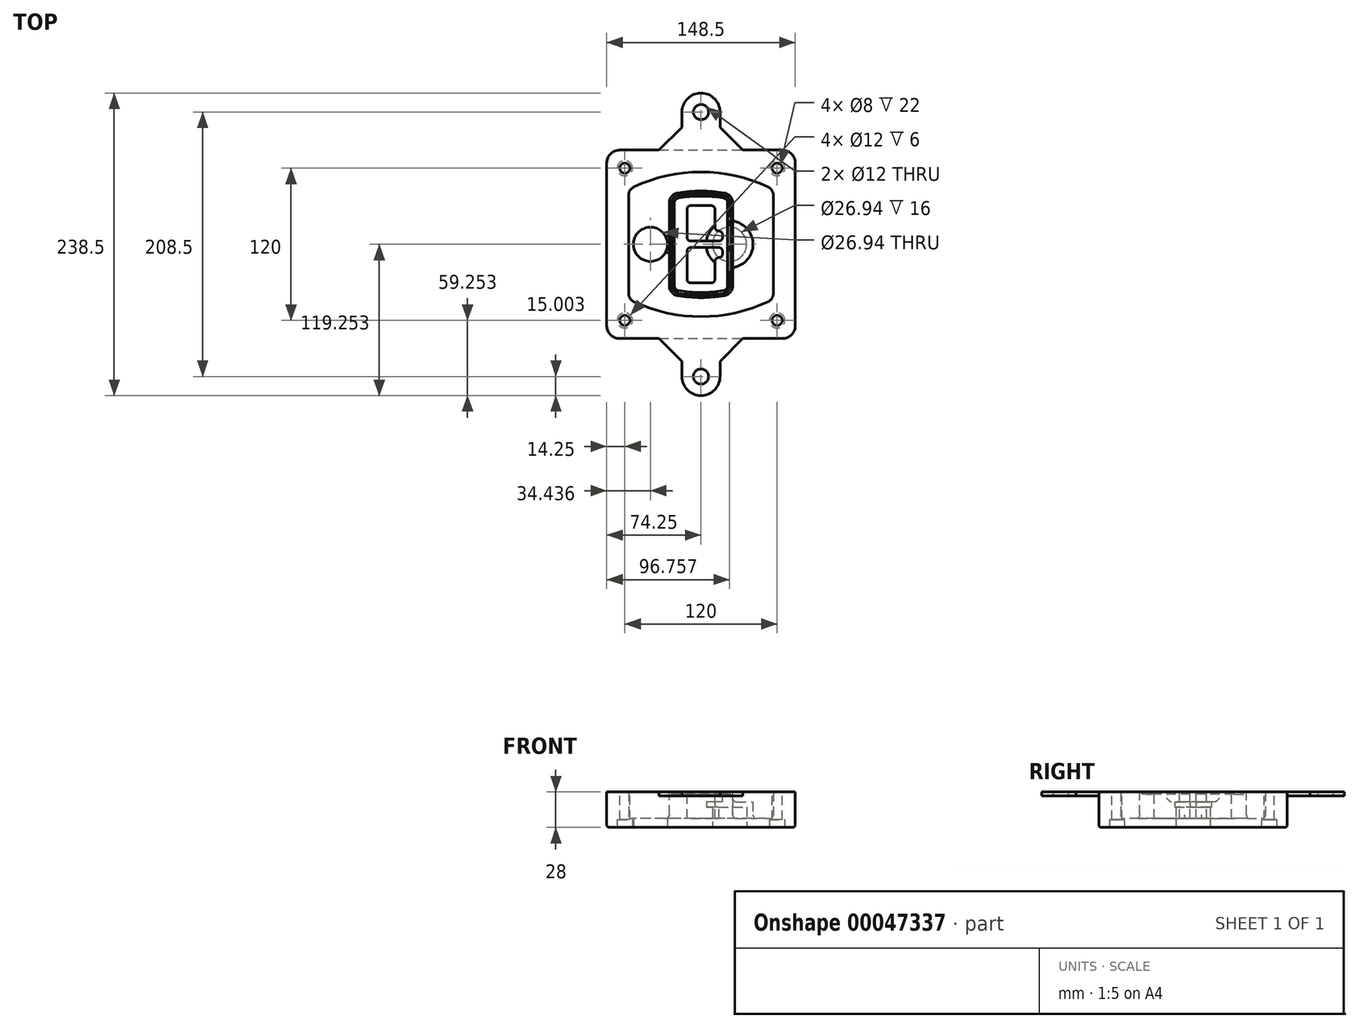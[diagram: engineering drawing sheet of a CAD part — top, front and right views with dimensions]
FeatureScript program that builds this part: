
annotation { "Feature Type Name" : "Feature", "Feature Type Description" : "" }
export const myFeature = defineFeature(function(context is Context, id is Id, definition is map)
    precondition{}
    {
        {
            var Q0;
            Q0=qCreatedBy(makeId("Top.planeOp"),FACE);
            var sketch = newSketch(context, id + "F0", { "sketchPlane" : qUnion([Q0])});
            skPoint(sketch, "E0.rect.middle", {"position": v(0, 0) * mm});
            skLineSegment(sketch, "E1.bottom", {"start": v(24.05, 28.38) * mm, "end": v(152.55, 28.38) * mm});
            skLineSegment(sketch, "E1.top", {"start": v(24.05, 176.88) * mm, "end": v(152.55, 176.88) * mm});
            skLineSegment(sketch, "E1.left", {"start": v(14.05, 38.38) * mm, "end": v(14.05, 166.88) * mm});
            skLineSegment(sketch, "E1.right", {"start": v(162.55, 38.38) * mm, "end": v(162.55, 166.88) * mm});
            skLineSegment(sketch, "E2", {"start": v(14.05, 176.88) * mm, "end": v(162.55, 28.38) * mm, "construction": true});
            skLineSegment(sketch, "E3", {"start": v(162.55, 176.88) * mm, "end": v(14.05, 28.38) * mm, "construction": true});
            skCircle(sketch, "E4", {"center": v(28.3, 162.63) * mm, "radius": 4 * mm});
            skCircle(sketch, "E5", {"center": v(148.3, 162.63) * mm, "radius": 4 * mm});
            skCircle(sketch, "E6", {"center": v(148.3, 42.63) * mm, "radius": 4 * mm});
            skCircle(sketch, "E7", {"center": v(28.3, 42.63) * mm, "radius": 4 * mm});
            skLineSegment(sketch, "E8", {"start": v(28.3, 162.63) * mm, "end": v(148.3, 162.63) * mm, "construction": true});
            skLineSegment(sketch, "E9", {"start": v(148.3, 162.63) * mm, "end": v(148.3, 42.63) * mm, "construction": true});
            skLineSegment(sketch, "E10", {"start": v(148.3, 42.63) * mm, "end": v(28.3, 42.63) * mm, "construction": true});
            skLineSegment(sketch, "E11", {"start": v(28.3, 42.63) * mm, "end": v(28.3, 162.63) * mm, "construction": true});
            skLineSegment(sketch, "E12", {"start": v(28.3, 141.46) * mm, "end": v(28.3, 63.8) * mm});
            skLineSegment(sketch, "E13", {"start": v(148.3, 141.46) * mm, "end": v(148.3, 63.8) * mm});
            skArc(sketch, "E14", {"start": v(142.56, 150.51) * mm, "mid": v(88.3, 162.63) * mm, "end": v(34.04, 150.51) * mm});
            skArc(sketch, "E15", {"start": v(34.04, 54.75) * mm, "mid": v(88.3, 42.63) * mm, "end": v(142.56, 54.75) * mm});
            skLineSegment(sketch, "E16", {"start": v(28.3, 102.63) * mm, "end": v(148.3, 102.63) * mm, "construction": true});
            skPoint(sketch, "E17.visualSharp", {"position": v(28.3, 57.63) * mm});
            skArc(sketch, "E17.filletArc", {"start": v(28.3, 63.8) * mm, "mid": v(29.86, 58.44) * mm, "end": v(34.04, 54.75) * mm});
            skPoint(sketch, "E18.visualSharp", {"position": v(28.3, 147.63) * mm});
            skArc(sketch, "E18.filletArc", {"start": v(34.04, 150.51) * mm, "mid": v(29.86, 146.82) * mm, "end": v(28.3, 141.46) * mm});
            skPoint(sketch, "E19.visualSharp", {"position": v(148.3, 147.63) * mm});
            skArc(sketch, "E19.filletArc", {"start": v(148.3, 141.46) * mm, "mid": v(146.74, 146.82) * mm, "end": v(142.56, 150.51) * mm});
            skPoint(sketch, "E20.visualSharp", {"position": v(148.3, 57.63) * mm});
            skArc(sketch, "E20.filletArc", {"start": v(142.56, 54.75) * mm, "mid": v(146.74, 58.44) * mm, "end": v(148.3, 63.8) * mm});
            skPoint(sketch, "E21.visualSharp", {"position": v(14.05, 176.88) * mm});
            skArc(sketch, "E21.filletArc", {"start": v(24.05, 176.88) * mm, "mid": v(16.98, 173.95) * mm, "end": v(14.05, 166.88) * mm});
            skPoint(sketch, "E22.visualSharp", {"position": v(162.55, 176.88) * mm});
            skArc(sketch, "E22.filletArc", {"start": v(162.55, 166.88) * mm, "mid": v(159.62, 173.95) * mm, "end": v(152.55, 176.88) * mm});
            skPoint(sketch, "E23.visualSharp", {"position": v(162.55, 28.38) * mm});
            skArc(sketch, "E23.filletArc", {"start": v(152.55, 28.38) * mm, "mid": v(159.62, 31.31) * mm, "end": v(162.55, 38.38) * mm});
            skPoint(sketch, "E24.visualSharp", {"position": v(14.05, 28.38) * mm});
            skArc(sketch, "E24.filletArc", {"start": v(14.05, 38.38) * mm, "mid": v(16.98, 31.31) * mm, "end": v(24.05, 28.38) * mm});
            skArc(sketch, "E25.0", {"start": v(145.3, 141.46) * mm, "mid": v(144.2, 145.22) * mm, "end": v(141.28, 147.8) * mm});
            skLineSegment(sketch, "E25.1", {"start": v(145.3, 141.46) * mm, "end": v(145.3, 63.8) * mm});
            skArc(sketch, "E25.2", {"start": v(141.28, 57.47) * mm, "mid": v(144.2, 60.05) * mm, "end": v(145.3, 63.8) * mm});
            skArc(sketch, "E25.3", {"start": v(35.32, 57.47) * mm, "mid": v(88.3, 45.63) * mm, "end": v(141.28, 57.47) * mm});
            skArc(sketch, "E25.4", {"start": v(31.3, 63.8) * mm, "mid": v(32.4, 60.05) * mm, "end": v(35.32, 57.47) * mm});
            skArc(sketch, "E25.5", {"start": v(141.28, 147.8) * mm, "mid": v(88.3, 159.63) * mm, "end": v(35.32, 147.8) * mm});
            skLineSegment(sketch, "E25.6", {"start": v(31.3, 141.46) * mm, "end": v(31.3, 63.8) * mm});
            skArc(sketch, "E25.7", {"start": v(35.32, 147.8) * mm, "mid": v(32.4, 145.22) * mm, "end": v(31.3, 141.46) * mm});
            skArc(sketch, "E26.0", {"start": v(32.34, 154.13) * mm, "mid": v(26.48, 148.97) * mm, "end": v(24.3, 141.46) * mm});
            skArc(sketch, "E26.1", {"start": v(144.26, 154.13) * mm, "mid": v(88.3, 166.63) * mm, "end": v(32.34, 154.13) * mm});
            skArc(sketch, "E26.2", {"start": v(152.3, 141.46) * mm, "mid": v(150.12, 148.97) * mm, "end": v(144.26, 154.13) * mm});
            skLineSegment(sketch, "E26.3", {"start": v(152.3, 141.46) * mm, "end": v(152.3, 63.8) * mm});
            skArc(sketch, "E26.4", {"start": v(144.26, 51.13) * mm, "mid": v(150.12, 56.3) * mm, "end": v(152.3, 63.8) * mm});
            skLineSegment(sketch, "E26.5", {"start": v(24.3, 141.46) * mm, "end": v(24.3, 63.8) * mm});
            skArc(sketch, "E26.6", {"start": v(32.34, 51.13) * mm, "mid": v(88.3, 38.63) * mm, "end": v(144.26, 51.13) * mm});
            skArc(sketch, "E26.7", {"start": v(24.3, 63.8) * mm, "mid": v(26.48, 56.3) * mm, "end": v(32.34, 51.13) * mm});
            skSolve(sketch);
        }
        {
            var Q0;
            Q0=makeQuery(id+"F0.imprint","IMPRINT",FACE,{"disambiguationData":[TD([[makeQuery(id+"F0.imprint","IMPRINT",EDGE,{"derivedFrom":sQuery(id+"F0.wireOp",EDGE,"E1.bottom")}),1.0]])]});
            var Q1;
            Q1=makeQuery(id+"F0.imprint","IMPRINT",FACE,{"disambiguationData":[TD([[makeQuery(id+"F0.imprint","IMPRINT",EDGE,{"derivedFrom":sQuery(id+"F0.wireOp",EDGE,"E12")}),1.0]])]});
            var Q2;
            Q2=makeQuery(id+"F0.imprint","IMPRINT",FACE,{"disambiguationData":[TD([[makeQuery(id+"F0.imprint","IMPRINT",EDGE,{"derivedFrom":sQuery(id+"F0.wireOp",EDGE,"E25.0")}),1.0]])]});
            var Q3;
            Q3=makeQuery(id+"F0.imprint","IMPRINT",FACE,{"disambiguationData":[TD([[makeQuery(id+"F0.imprint","IMPRINT",EDGE,{"derivedFrom":sQuery(id+"F0.wireOp",EDGE,"E12")}),-1.0]])]});
            extrude(context, id + "F1", {"entities" : qUnion([Q0, Q1, Q2, Q3]), "oppositeDirection" : true, "depth" : 25 * mm});
        }
        {
            var Q0;
            Q0=makeQuery(id+"F0.imprint","IMPRINT",FACE,{"disambiguationData":[TD([[makeQuery(id+"F0.imprint","IMPRINT",EDGE,{"derivedFrom":sQuery(id+"F0.wireOp",EDGE,"E12")}),1.0]])]});
            extrude(context, id + "F2", {"entities" : qUnion([Q0]), "operationType" : NewBodyOperationType.ADD, "depth" : 3 * mm});
        }
        {
            var Q0;
            Q0=makeQuery(id+"F0.imprint","IMPRINT",FACE,{"disambiguationData":[TD([[makeQuery(id+"F0.imprint","IMPRINT",EDGE,{"derivedFrom":sQuery(id+"F0.wireOp",EDGE,"E25.0")}),1.0]])]});
            extrude(context, id + "F3", {"entities" : qUnion([Q0]), "operationType" : NewBodyOperationType.REMOVE, "oppositeDirection" : true, "depth" : 18 * mm});
        }
        {
            var Q0;
            Q0=makeQuery(id+"F2.opExtrude","CAP_FACE",FACE,{"disambiguationData":[OSD([sQuery(id+"F0.wireOp",EDGE,"E12"),sQuery(id+"F0.wireOp",EDGE,"E13"),sQuery(id+"F0.wireOp",EDGE,"E14"),sQuery(id+"F0.wireOp",EDGE,"E15"),sQuery(id+"F0.wireOp",EDGE,"E17.filletArc"),sQuery(id+"F0.wireOp",EDGE,"E18.filletArc"),sQuery(id+"F0.wireOp",EDGE,"E19.filletArc"),sQuery(id+"F0.wireOp",EDGE,"E20.filletArc"),sQuery(id+"F0.wireOp",EDGE,"E25.0"),sQuery(id+"F0.wireOp",EDGE,"E25.1"),sQuery(id+"F0.wireOp",EDGE,"E25.2"),sQuery(id+"F0.wireOp",EDGE,"E25.3"),sQuery(id+"F0.wireOp",EDGE,"E25.4"),sQuery(id+"F0.wireOp",EDGE,"E25.5"),sQuery(id+"F0.wireOp",EDGE,"E25.6"),sQuery(id+"F0.wireOp",EDGE,"E25.7")])],"isStart":false});
            var sketch = newSketch(context, id + "F4", { "sketchPlane" : qUnion([Q0])});
            skArc(sketch, "E27.0", {"start": v(69.96, 62.18) * mm, "mid": v(88.3, 60.63) * mm, "end": v(106.64, 62.18) * mm});
            skArc(sketch, "E28.0", {"start": v(106.64, 143.09) * mm, "mid": v(88.3, 144.63) * mm, "end": v(69.96, 143.09) * mm});
            skLineSegment(sketch, "E29", {"start": v(63.3, 135.2) * mm, "end": v(63.3, 70.07) * mm});
            skLineSegment(sketch, "E30", {"start": v(113.3, 135.2) * mm, "end": v(113.3, 70.07) * mm});
            skLineSegment(sketch, "E31", {"start": v(63.3, 141.74) * mm, "end": v(113.3, 141.74) * mm, "construction": true});
            skLineSegment(sketch, "E32", {"start": v(63.3, 63.52) * mm, "end": v(113.3, 63.52) * mm, "construction": true});
            skPoint(sketch, "E33.visualSharp", {"position": v(63.3, 141.74) * mm});
            skArc(sketch, "E33.filletArc", {"start": v(69.96, 143.09) * mm, "mid": v(65.19, 140.36) * mm, "end": v(63.3, 135.2) * mm});
            skPoint(sketch, "E34.visualSharp", {"position": v(113.3, 141.74) * mm});
            skArc(sketch, "E34.filletArc", {"start": v(113.3, 135.2) * mm, "mid": v(111.41, 140.36) * mm, "end": v(106.64, 143.09) * mm});
            skPoint(sketch, "E35.visualSharp", {"position": v(113.3, 63.52) * mm});
            skArc(sketch, "E35.filletArc", {"start": v(106.64, 62.18) * mm, "mid": v(111.41, 64.9) * mm, "end": v(113.3, 70.07) * mm});
            skPoint(sketch, "E36.visualSharp", {"position": v(63.3, 63.52) * mm});
            skArc(sketch, "E36.filletArc", {"start": v(63.3, 70.07) * mm, "mid": v(65.19, 64.9) * mm, "end": v(69.96, 62.18) * mm});
            skArc(sketch, "E37.0", {"start": v(141.28, 147.8) * mm, "mid": v(88.3, 159.63) * mm, "end": v(35.32, 147.8) * mm});
            skArc(sketch, "E37.1", {"start": v(35.32, 147.8) * mm, "mid": v(32.4, 145.22) * mm, "end": v(31.3, 141.46) * mm});
            skLineSegment(sketch, "E37.2", {"start": v(31.3, 141.46) * mm, "end": v(31.3, 63.8) * mm});
            skArc(sketch, "E37.3", {"start": v(31.3, 63.8) * mm, "mid": v(32.4, 60.05) * mm, "end": v(35.32, 57.47) * mm});
            skArc(sketch, "E37.4", {"start": v(35.32, 57.47) * mm, "mid": v(88.3, 45.63) * mm, "end": v(141.28, 57.47) * mm});
            skArc(sketch, "E37.5", {"start": v(141.28, 57.47) * mm, "mid": v(144.2, 60.05) * mm, "end": v(145.3, 63.8) * mm});
            skLineSegment(sketch, "E37.6", {"start": v(145.3, 141.46) * mm, "end": v(145.3, 63.8) * mm});
            skArc(sketch, "E37.7", {"start": v(145.3, 141.46) * mm, "mid": v(144.2, 145.22) * mm, "end": v(141.28, 147.8) * mm});
            skLineSegment(sketch, "E38.0", {"start": v(111.3, 135.2) * mm, "end": v(111.3, 70.07) * mm});
            skArc(sketch, "E38.1", {"start": v(106.3, 64.15) * mm, "mid": v(109.88, 66.2) * mm, "end": v(111.3, 70.07) * mm});
            skArc(sketch, "E38.2", {"start": v(70.3, 64.15) * mm, "mid": v(88.3, 62.63) * mm, "end": v(106.3, 64.15) * mm});
            skArc(sketch, "E38.3", {"start": v(65.3, 70.07) * mm, "mid": v(66.72, 66.2) * mm, "end": v(70.3, 64.15) * mm});
            skLineSegment(sketch, "E38.4", {"start": v(65.3, 135.2) * mm, "end": v(65.3, 70.07) * mm});
            skArc(sketch, "E38.5", {"start": v(111.3, 135.2) * mm, "mid": v(109.88, 139.07) * mm, "end": v(106.3, 141.11) * mm});
            skArc(sketch, "E38.6", {"start": v(70.3, 141.11) * mm, "mid": v(66.72, 139.07) * mm, "end": v(65.3, 135.2) * mm});
            skArc(sketch, "E38.7", {"start": v(106.3, 141.11) * mm, "mid": v(88.3, 142.63) * mm, "end": v(70.3, 141.11) * mm});
            skArc(sketch, "E39.0", {"start": v(109.3, 135.2) * mm, "mid": v(108.36, 137.78) * mm, "end": v(105.97, 139.14) * mm});
            skLineSegment(sketch, "E39.1", {"start": v(109.3, 135.2) * mm, "end": v(109.3, 70.07) * mm});
            skArc(sketch, "E39.2", {"start": v(105.97, 66.12) * mm, "mid": v(108.36, 67.49) * mm, "end": v(109.3, 70.07) * mm});
            skArc(sketch, "E39.3", {"start": v(70.63, 66.12) * mm, "mid": v(88.3, 64.63) * mm, "end": v(105.97, 66.12) * mm});
            skArc(sketch, "E39.4", {"start": v(67.3, 70.07) * mm, "mid": v(68.24, 67.49) * mm, "end": v(70.63, 66.12) * mm});
            skArc(sketch, "E39.5", {"start": v(105.97, 139.14) * mm, "mid": v(88.3, 140.63) * mm, "end": v(70.63, 139.14) * mm});
            skLineSegment(sketch, "E39.6", {"start": v(67.3, 135.2) * mm, "end": v(67.3, 70.07) * mm});
            skArc(sketch, "E39.7", {"start": v(70.63, 139.14) * mm, "mid": v(68.24, 137.78) * mm, "end": v(67.3, 135.2) * mm});
            skLineSegment(sketch, "E40", {"start": v(63.3, 102.63) * mm, "end": v(113.3, 102.63) * mm, "construction": true});
            skLineSegment(sketch, "E41", {"start": v(77.3, 108.13) * mm, "end": v(77.3, 130.13) * mm});
            skLineSegment(sketch, "E42", {"start": v(80.3, 133.13) * mm, "end": v(96.3, 133.13) * mm});
            skLineSegment(sketch, "E43", {"start": v(99.3, 130.13) * mm, "end": v(99.3, 116.13) * mm});
            skLineSegment(sketch, "E44", {"start": v(102.3, 113.13) * mm, "end": v(102.3, 113.13) * mm});
            skLineSegment(sketch, "E45", {"start": v(105.3, 110.13) * mm, "end": v(105.3, 108.13) * mm});
            skLineSegment(sketch, "E46", {"start": v(102.3, 105.13) * mm, "end": v(80.3, 105.13) * mm});
            skPoint(sketch, "E47.visualSharp", {"position": v(77.3, 133.13) * mm});
            skArc(sketch, "E47.filletArc", {"start": v(80.3, 133.13) * mm, "mid": v(78.18, 132.25) * mm, "end": v(77.3, 130.13) * mm});
            skPoint(sketch, "E48.visualSharp", {"position": v(99.3, 133.13) * mm});
            skArc(sketch, "E48.filletArc", {"start": v(99.3, 130.13) * mm, "mid": v(98.42, 132.25) * mm, "end": v(96.3, 133.13) * mm});
            skPoint(sketch, "E49.visualSharp", {"position": v(99.3, 113.13) * mm});
            skArc(sketch, "E49.filletArc", {"start": v(99.3, 116.13) * mm, "mid": v(100.18, 114.01) * mm, "end": v(102.3, 113.13) * mm});
            skPoint(sketch, "E50.visualSharp", {"position": v(105.3, 113.13) * mm});
            skArc(sketch, "E50.filletArc", {"start": v(105.3, 110.13) * mm, "mid": v(104.42, 112.25) * mm, "end": v(102.3, 113.13) * mm});
            skPoint(sketch, "E51.visualSharp", {"position": v(105.3, 105.13) * mm});
            skArc(sketch, "E51.filletArc", {"start": v(102.3, 105.13) * mm, "mid": v(104.42, 106.01) * mm, "end": v(105.3, 108.13) * mm});
            skPoint(sketch, "E52.visualSharp", {"position": v(77.3, 105.13) * mm});
            skArc(sketch, "E52.filletArc", {"start": v(77.3, 108.13) * mm, "mid": v(78.18, 106.01) * mm, "end": v(80.3, 105.13) * mm});
            skLineSegment(sketch, "E53.0.MirrorCS", {"start": v(102.3, 100.13) * mm, "end": v(80.3, 100.13) * mm});
            skArc(sketch, "E54.0.MirrorCS", {"start": v(77.3, 97.13) * mm, "mid": v(78.18, 99.25) * mm, "end": v(80.3, 100.13) * mm});
            skLineSegment(sketch, "E55.0.MirrorCS", {"start": v(77.3, 97.13) * mm, "end": v(77.3, 75.13) * mm});
            skArc(sketch, "E56.0.MirrorCS", {"start": v(80.3, 72.13) * mm, "mid": v(78.18, 73.01) * mm, "end": v(77.3, 75.13) * mm});
            skLineSegment(sketch, "E57.0.MirrorCS", {"start": v(80.3, 72.13) * mm, "end": v(96.3, 72.13) * mm});
            skArc(sketch, "E58.0.MirrorCS", {"start": v(99.3, 75.13) * mm, "mid": v(98.42, 73.01) * mm, "end": v(96.3, 72.13) * mm});
            skLineSegment(sketch, "E59.0.MirrorCS", {"start": v(99.3, 75.13) * mm, "end": v(99.3, 89.13) * mm});
            skArc(sketch, "E60.0.MirrorCS", {"start": v(99.3, 89.13) * mm, "mid": v(100.18, 91.25) * mm, "end": v(102.3, 92.13) * mm});
            skArc(sketch, "E61.0.MirrorCS", {"start": v(105.3, 95.13) * mm, "mid": v(104.42, 93.01) * mm, "end": v(102.3, 92.13) * mm});
            skLineSegment(sketch, "E62.0.MirrorCS", {"start": v(105.3, 95.13) * mm, "end": v(105.3, 97.13) * mm});
            skArc(sketch, "E63.0.MirrorCS", {"start": v(102.3, 100.13) * mm, "mid": v(104.42, 99.25) * mm, "end": v(105.3, 97.13) * mm});
            skSolve(sketch);
        }
        {
            var Q0;
            Q0=makeQuery(id+"F4.imprint","IMPRINT",FACE,{"disambiguationData":[TD([[makeQuery(id+"F4.imprint","IMPRINT",EDGE,{"derivedFrom":sQuery(id+"F4.wireOp",EDGE,"E27.0")}),1.0]])]});
            var Q1;
            Q1=makeQuery(id+"F4.imprint","IMPRINT",FACE,{"disambiguationData":[TD([[makeQuery(id+"F4.imprint","IMPRINT",EDGE,{"derivedFrom":sQuery(id+"F4.wireOp",EDGE,"E38.0")}),-1.0]])]});
            var Q2;
            Q2=makeQuery(id+"F4.imprint","IMPRINT",FACE,{"disambiguationData":[TD([[makeQuery(id+"F4.imprint","IMPRINT",EDGE,{"derivedFrom":sQuery(id+"F4.wireOp",EDGE,"E39.0")}),1.0]])]});
            extrude(context, id + "F5", {"entities" : qUnion([Q0, Q1, Q2]), "operationType" : NewBodyOperationType.ADD, "endBound" : BoundingType.UP_TO_NEXT, "oppositeDirection" : true, "depth" : 25 * mm});
        }
        {
            var Q0;
            Q0=makeQuery(id+"F4.imprint","IMPRINT",FACE,{"disambiguationData":[TD([[makeQuery(id+"F4.imprint","IMPRINT",EDGE,{"derivedFrom":sQuery(id+"F4.wireOp",EDGE,"E38.0")}),-1.0]])]});
            extrude(context, id + "F6", {"entities" : qUnion([Q0]), "operationType" : NewBodyOperationType.REMOVE, "oppositeDirection" : true, "depth" : 2 * mm});
        }
        {
            var Q0;
            Q0=makeQuery(id+"F1.opExtrude","CAP_FACE",FACE,{"disambiguationData":[OSD([sQuery(id+"F0.wireOp",EDGE,"E1.bottom"),sQuery(id+"F0.wireOp",EDGE,"E1.top"),sQuery(id+"F0.wireOp",EDGE,"E1.left"),sQuery(id+"F0.wireOp",EDGE,"E1.right"),sQuery(id+"F0.wireOp",EDGE,"E4"),sQuery(id+"F0.wireOp",EDGE,"E5"),sQuery(id+"F0.wireOp",EDGE,"E6"),sQuery(id+"F0.wireOp",EDGE,"E7"),sQuery(id+"F0.wireOp",EDGE,"E21.filletArc"),sQuery(id+"F0.wireOp",EDGE,"E22.filletArc"),sQuery(id+"F0.wireOp",EDGE,"E23.filletArc"),sQuery(id+"F0.wireOp",EDGE,"E24.filletArc")])],"isStart":false});
            var sketch = newSketch(context, id + "F7", { "sketchPlane" : qUnion([Q0])});
            skCircle(sketch, "E64", {"center": v(110.8, -102.63) * mm, "radius": 13.47 * mm});
            skCircle(sketch, "E65", {"center": v(48.49, -102.63) * mm, "radius": 13.47 * mm});
            skLineSegment(sketch, "E66", {"start": v(162.55, -102.63) * mm, "end": v(14.05, -102.63) * mm});
            skCircle(sketch, "E67", {"center": v(110.8, -102.63) * mm, "radius": 18.47 * mm});
            skCircle(sketch, "E68", {"center": v(148.3, -162.63) * mm, "radius": 6 * mm});
            skCircle(sketch, "E69", {"center": v(28.3, -162.63) * mm, "radius": 6 * mm});
            skCircle(sketch, "E70", {"center": v(28.3, -42.63) * mm, "radius": 6 * mm});
            skCircle(sketch, "E71", {"center": v(148.3, -42.63) * mm, "radius": 6 * mm});
            skSolve(sketch);
        }
        {
            var Q0;
            {var subQ1=sQuery(id+"F7.wireOp",EDGE,"E66");var subQ4=sQuery(id+"F7.wireOp",EDGE,"E64");var subQ6=makeQuery(id+"F7.imprint","INTERSECT",VERTEX,{"disambiguationData":[OD(0.0)],"derivedFrom":[subQ4,subQ1]});Q0=makeQuery(id+"F7.imprint","IMPRINT",FACE,{"disambiguationData":[TD([[makeQuery(id+"F7.imprint","IMPRINT",EDGE,{"disambiguationData":[TD([[subQ6,-1.0]])],"derivedFrom":subQ4}),-1.0]])]});}
            var Q1;
            {var subQ0=sQuery(id+"F7.wireOp",EDGE,"E66");var subQ1=sQuery(id+"F7.wireOp",EDGE,"E64");var subQ3=makeQuery(id+"F7.imprint","INTERSECT",VERTEX,{"disambiguationData":[OD(0.0)],"derivedFrom":[subQ1,subQ0]});Q1=makeQuery(id+"F7.imprint","IMPRINT",FACE,{"disambiguationData":[TD([[makeQuery(id+"F7.imprint","IMPRINT",EDGE,{"disambiguationData":[TD([[subQ3,-1.0]])],"derivedFrom":subQ1}),1.0]])]});}
            var Q2;
            {var subQ0=sQuery(id+"F7.wireOp",EDGE,"E66");var subQ1=sQuery(id+"F7.wireOp",EDGE,"E64");var subQ3=makeQuery(id+"F7.imprint","INTERSECT",VERTEX,{"disambiguationData":[OD(0.0)],"derivedFrom":[subQ1,subQ0]});Q2=makeQuery(id+"F7.imprint","IMPRINT",FACE,{"disambiguationData":[TD([[makeQuery(id+"F7.imprint","IMPRINT",EDGE,{"disambiguationData":[TD([[subQ3,1.0]])],"derivedFrom":subQ1}),1.0]])]});}
            var Q3;
            {var subQ1=sQuery(id+"F7.wireOp",EDGE,"E66");var subQ4=sQuery(id+"F7.wireOp",EDGE,"E64");var subQ6=makeQuery(id+"F7.imprint","INTERSECT",VERTEX,{"disambiguationData":[OD(0.0)],"derivedFrom":[subQ4,subQ1]});Q3=makeQuery(id+"F7.imprint","IMPRINT",FACE,{"disambiguationData":[TD([[makeQuery(id+"F7.imprint","IMPRINT",EDGE,{"disambiguationData":[TD([[subQ6,1.0]])],"derivedFrom":subQ4}),-1.0]])]});}
            extrude(context, id + "F8", {"entities" : qUnion([Q0, Q1, Q2, Q3]), "operationType" : NewBodyOperationType.ADD, "oppositeDirection" : true, "depth" : 20 * mm});
        }
        {
            var Q0;
            {var subQ0=sQuery(id+"F7.wireOp",EDGE,"E66");var subQ1=sQuery(id+"F7.wireOp",EDGE,"E64");var subQ3=makeQuery(id+"F7.imprint","INTERSECT",VERTEX,{"disambiguationData":[OD(0.0)],"derivedFrom":[subQ1,subQ0]});Q0=makeQuery(id+"F7.imprint","IMPRINT",FACE,{"disambiguationData":[TD([[makeQuery(id+"F7.imprint","IMPRINT",EDGE,{"disambiguationData":[TD([[subQ3,-1.0]])],"derivedFrom":subQ1}),1.0]])]});}
            var Q1;
            {var subQ0=sQuery(id+"F7.wireOp",EDGE,"E66");var subQ1=sQuery(id+"F7.wireOp",EDGE,"E64");var subQ3=makeQuery(id+"F7.imprint","INTERSECT",VERTEX,{"disambiguationData":[OD(0.0)],"derivedFrom":[subQ1,subQ0]});Q1=makeQuery(id+"F7.imprint","IMPRINT",FACE,{"disambiguationData":[TD([[makeQuery(id+"F7.imprint","IMPRINT",EDGE,{"disambiguationData":[TD([[subQ3,1.0]])],"derivedFrom":subQ1}),1.0]])]});}
            extrude(context, id + "F9", {"entities" : qUnion([Q0, Q1]), "operationType" : NewBodyOperationType.REMOVE, "oppositeDirection" : true, "depth" : 16 * mm});
        }
        {
            var Q0;
            {var subQ0=sQuery(id+"F7.wireOp",EDGE,"E66");var subQ1=sQuery(id+"F7.wireOp",EDGE,"E65");var subQ3=makeQuery(id+"F7.imprint","INTERSECT",VERTEX,{"disambiguationData":[OD(0.0)],"derivedFrom":[subQ1,subQ0]});Q0=makeQuery(id+"F7.imprint","IMPRINT",FACE,{"disambiguationData":[TD([[makeQuery(id+"F7.imprint","IMPRINT",EDGE,{"disambiguationData":[TD([[subQ3,-1.0]])],"derivedFrom":subQ1}),1.0]])]});}
            var Q1;
            {var subQ0=sQuery(id+"F7.wireOp",EDGE,"E66");var subQ1=sQuery(id+"F7.wireOp",EDGE,"E65");var subQ3=makeQuery(id+"F7.imprint","INTERSECT",VERTEX,{"disambiguationData":[OD(0.0)],"derivedFrom":[subQ1,subQ0]});Q1=makeQuery(id+"F7.imprint","IMPRINT",FACE,{"disambiguationData":[TD([[makeQuery(id+"F7.imprint","IMPRINT",EDGE,{"disambiguationData":[TD([[subQ3,1.0]])],"derivedFrom":subQ1}),1.0]])]});}
            extrude(context, id + "F10", {"entities" : qUnion([Q0, Q1]), "operationType" : NewBodyOperationType.REMOVE, "oppositeDirection" : true, "depth" : 25 * mm});
        }
        {
            var Q0;
            Q0=makeQuery(id+"F7.imprint","IMPRINT",FACE,{"disambiguationData":[TD([[makeQuery(id+"F7.imprint","IMPRINT",EDGE,{"derivedFrom":sQuery(id+"F7.wireOp",EDGE,"E68")}),1.0]])]});
            var Q1;
            Q1=makeQuery(id+"F7.imprint","IMPRINT",FACE,{"disambiguationData":[TD([[makeQuery(id+"F7.imprint","IMPRINT",EDGE,{"derivedFrom":makeQuery(id+"F1.opExtrude","CAP_EDGE",EDGE,{"disambiguationData":[OSD([sQuery(id+"F0.wireOp",EDGE,"E5")])],"isStart":false})}),-1.0]])]});
            var Q2;
            Q2=makeQuery(id+"F7.imprint","IMPRINT",FACE,{"disambiguationData":[TD([[makeQuery(id+"F7.imprint","IMPRINT",EDGE,{"derivedFrom":sQuery(id+"F7.wireOp",EDGE,"E69")}),1.0]])]});
            var Q3;
            Q3=makeQuery(id+"F7.imprint","IMPRINT",FACE,{"disambiguationData":[TD([[makeQuery(id+"F7.imprint","IMPRINT",EDGE,{"derivedFrom":makeQuery(id+"F1.opExtrude","CAP_EDGE",EDGE,{"disambiguationData":[OSD([sQuery(id+"F0.wireOp",EDGE,"E4")])],"isStart":false})}),-1.0]])]});
            var Q4;
            Q4=makeQuery(id+"F7.imprint","IMPRINT",FACE,{"disambiguationData":[TD([[makeQuery(id+"F7.imprint","IMPRINT",EDGE,{"derivedFrom":sQuery(id+"F7.wireOp",EDGE,"E70")}),1.0]])]});
            var Q5;
            Q5=makeQuery(id+"F7.imprint","IMPRINT",FACE,{"disambiguationData":[TD([[makeQuery(id+"F7.imprint","IMPRINT",EDGE,{"derivedFrom":makeQuery(id+"F1.opExtrude","CAP_EDGE",EDGE,{"disambiguationData":[OSD([sQuery(id+"F0.wireOp",EDGE,"E7")])],"isStart":false})}),-1.0]])]});
            var Q6;
            Q6=makeQuery(id+"F7.imprint","IMPRINT",FACE,{"disambiguationData":[TD([[makeQuery(id+"F7.imprint","IMPRINT",EDGE,{"derivedFrom":sQuery(id+"F7.wireOp",EDGE,"E71")}),1.0]])]});
            var Q7;
            Q7=makeQuery(id+"F7.imprint","IMPRINT",FACE,{"disambiguationData":[TD([[makeQuery(id+"F7.imprint","IMPRINT",EDGE,{"derivedFrom":makeQuery(id+"F1.opExtrude","CAP_EDGE",EDGE,{"disambiguationData":[OSD([sQuery(id+"F0.wireOp",EDGE,"E6")])],"isStart":false})}),-1.0]])]});
            extrude(context, id + "F11", {"entities" : qUnion([Q0, Q1, Q2, Q3, Q4, Q5, Q6, Q7]), "operationType" : NewBodyOperationType.REMOVE, "oppositeDirection" : true, "depth" : 6 * mm});
        }
        {
            var Q0;
            Q0=makeQuery(id+"F9.boolean.opBoolean","COPY",FACE,{"derivedFrom":makeQuery(id+"F9.opExtrude","CAP_FACE",FACE,{"disambiguationData":[OSD([sQuery(id+"F7.wireOp",EDGE,"E64")])],"isStart":false})});
            var sketch = newSketch(context, id + "F12", { "sketchPlane" : qUnion([Q0])});
            skArc(sketch, "E72.0", {"start": v(99.3, -88.19) * mm, "mid": v(94.75, -93.5) * mm, "end": v(92.5, -100.13) * mm});
            skArc(sketch, "E72.1", {"start": v(92.5, -105.13) * mm, "mid": v(94.75, -111.76) * mm, "end": v(99.3, -117.08) * mm});
            skLineSegment(sketch, "E73", {"start": v(92.5, -105.13) * mm, "end": v(102.3, -105.13) * mm});
            skLineSegment(sketch, "E74.0", {"start": v(102.3, -100.13) * mm, "end": v(92.5, -100.13) * mm});
            skArc(sketch, "E74.1", {"start": v(102.3, -100.13) * mm, "mid": v(104.42, -99.25) * mm, "end": v(105.3, -97.13) * mm});
            skLineSegment(sketch, "E74.2", {"start": v(105.3, -95.13) * mm, "end": v(105.3, -97.13) * mm});
            skArc(sketch, "E74.3", {"start": v(105.3, -95.13) * mm, "mid": v(104.42, -93.01) * mm, "end": v(102.3, -92.13) * mm});
            skArc(sketch, "E74.4", {"start": v(99.3, -89.13) * mm, "mid": v(100.18, -91.25) * mm, "end": v(102.3, -92.13) * mm});
            skLineSegment(sketch, "E74.5", {"start": v(99.3, -88.19) * mm, "end": v(99.3, -89.13) * mm});
            skLineSegment(sketch, "E74.7", {"start": v(102.3, -105.13) * mm, "end": v(92.5, -105.13) * mm});
            skArc(sketch, "E74.8", {"start": v(102.3, -105.13) * mm, "mid": v(104.42, -106.01) * mm, "end": v(105.3, -108.13) * mm});
            skLineSegment(sketch, "E74.9", {"start": v(105.3, -110.13) * mm, "end": v(105.3, -108.13) * mm});
            skArc(sketch, "E74.10", {"start": v(105.3, -110.13) * mm, "mid": v(104.42, -112.25) * mm, "end": v(102.3, -113.13) * mm});
            skArc(sketch, "E74.11", {"start": v(99.3, -116.13) * mm, "mid": v(100.18, -114.01) * mm, "end": v(102.3, -113.13) * mm});
            skLineSegment(sketch, "E74.12", {"start": v(99.3, -117.08) * mm, "end": v(99.3, -116.13) * mm});
            skPoint(sketch, "E75.orphan", {"position": v(99.3, -130.13) * mm});
            skPoint(sketch, "E76.orphan", {"position": v(80.3, -105.13) * mm});
            skPoint(sketch, "E77.orphan", {"position": v(80.3, -100.13) * mm});
            skPoint(sketch, "E78.orphan", {"position": v(99.3, -75.13) * mm});
            skSolve(sketch);
        }
        {
            var Q0;
            {var subQ7=sQuery(id+"F12.wireOp",EDGE,"E72.0");var subQ14=sQuery(id+"F12.wireOp",EDGE,"E72.1");var subQ16=sQuery(id+"F12.wireOp",EDGE,"E74.1");var subQ18=sQuery(id+"F12.wireOp",EDGE,"E74.8");Q0=qUnion([makeQuery(id+"F12.imprint","IMPRINT",FACE,{"disambiguationData":[TD([[makeQuery(id+"F12.imprint","IMPRINT",EDGE,{"derivedFrom":subQ7}),1.0]])]}),makeQuery(id+"F12.imprint","IMPRINT",FACE,{"disambiguationData":[TD([[makeQuery(id+"F12.imprint","IMPRINT",EDGE,{"derivedFrom":subQ14}),1.0]])]}),makeQuery(id+"F12.imprint","IMPRINT",FACE,{"disambiguationData":[TD([[makeQuery(id+"F12.imprint","IMPRINT",EDGE,{"derivedFrom":subQ16}),1.0]])]}),makeQuery(id+"F12.imprint","IMPRINT",FACE,{"disambiguationData":[TD([[makeQuery(id+"F12.imprint","IMPRINT",EDGE,{"derivedFrom":subQ18}),-1.0]])]})]);}
            var Q1;
            Q1=makeQuery(id+"F5.boolean.opBoolean","SPLIT",FACE,{"disambiguationData":[TD([makeQuery(id+"F5.opExtrude","SWEPT_FACE",FACE,{"disambiguationData":[OSD([sQuery(id+"F4.wireOp",EDGE,"E41")])]})])],"derivedFrom":makeQuery(id+"F3.boolean.opBoolean","COPY",FACE,{"derivedFrom":makeQuery(id+"F3.opExtrude","CAP_FACE",FACE,{"disambiguationData":[OSD([sQuery(id+"F0.wireOp",EDGE,"E25.0"),sQuery(id+"F0.wireOp",EDGE,"E25.1"),sQuery(id+"F0.wireOp",EDGE,"E25.2"),sQuery(id+"F0.wireOp",EDGE,"E25.3"),sQuery(id+"F0.wireOp",EDGE,"E25.4"),sQuery(id+"F0.wireOp",EDGE,"E25.5"),sQuery(id+"F0.wireOp",EDGE,"E25.6"),sQuery(id+"F0.wireOp",EDGE,"E25.7")])],"isStart":false})})});
            extrude(context, id + "F13", {"entities" : qUnion([Q0]), "operationType" : NewBodyOperationType.REMOVE, "endBound" : BoundingType.UP_TO_SURFACE, "endBoundEntityFace" : qUnion([Q1]), "depth" : 25 * mm});
        }
        {
            var Q0;
            Q0=makeQuery(id+"F3.boolean.opBoolean","COPY",EDGE,{"derivedFrom":makeQuery(id+"F3.opExtrude","CAP_EDGE",EDGE,{"disambiguationData":[OSD([sQuery(id+"F0.wireOp",EDGE,"E25.6")])],"isStart":false})});
            var Q1;
            Q1=makeQuery(id+"F8.boolean.opBoolean","INTERSECT",EDGE,{"derivedFrom":[makeQuery(id+"F5.opExtrude","SWEPT_FACE",FACE,{"disambiguationData":[OSD([sQuery(id+"F4.wireOp",EDGE,"E30")])]}),makeQuery(id+"F8.opExtrude","CAP_FACE",FACE,{"disambiguationData":[OSD([sQuery(id+"F7.wireOp",EDGE,"E67")])],"isStart":false})]});
            var Q2;
            Q2=makeQuery(id+"F8.boolean.opBoolean","INTERSECT",EDGE,{"disambiguationData":[OD(1.0)],"derivedFrom":[makeQuery(id+"F5.opExtrude","SWEPT_FACE",FACE,{"disambiguationData":[OSD([sQuery(id+"F4.wireOp",EDGE,"E30")])]}),makeQuery(id+"F8.opExtrude","SWEPT_FACE",FACE,{"disambiguationData":[OSD([sQuery(id+"F7.wireOp",EDGE,"E67")])]})]});
            var Q3;
            {var subQ0=sQuery(id+"F4.wireOp",EDGE,"E30");Q3=makeQuery(id+"F8.boolean.opBoolean","SPLIT",EDGE,{"disambiguationData":[TD([makeQuery(id+"F5.opExtrude","SWEPT_FACE",FACE,{"disambiguationData":[OSD([sQuery(id+"F4.wireOp",EDGE,"E35.filletArc")])]})])],"derivedFrom":makeQuery(id+"F5.opExtrude","CAP_EDGE",EDGE,{"disambiguationData":[OSD([subQ0])],"isStart":false})});}
            var Q4;
            {var subQ0=sQuery(id+"F0.wireOp",EDGE,"E25.7");var subQ1=sQuery(id+"F0.wireOp",EDGE,"E25.1");var subQ2=sQuery(id+"F0.wireOp",EDGE,"E25.6");var subQ3=sQuery(id+"F0.wireOp",EDGE,"E25.5");var subQ4=sQuery(id+"F0.wireOp",EDGE,"E25.4");var subQ5=sQuery(id+"F0.wireOp",EDGE,"E25.0");var subQ6=sQuery(id+"F0.wireOp",EDGE,"E25.2");var subQ7=sQuery(id+"F0.wireOp",EDGE,"E25.3");Q4=makeQuery(id+"F8.boolean.opBoolean","INTERSECT",EDGE,{"derivedFrom":[makeQuery(id+"F5.boolean.opBoolean","SPLIT",FACE,{"disambiguationData":[TD([makeQuery(id+"F2.opExtrude","SWEPT_FACE",FACE,{"disambiguationData":[OSD([subQ5])]})])],"derivedFrom":makeQuery(id+"F3.boolean.opBoolean","COPY",FACE,{"derivedFrom":makeQuery(id+"F3.opExtrude","CAP_FACE",FACE,{"disambiguationData":[OSD([subQ5,subQ1,subQ6,subQ7,subQ4,subQ3,subQ2,subQ0])],"isStart":false})})}),makeQuery(id+"F8.opExtrude","SWEPT_FACE",FACE,{"disambiguationData":[OSD([sQuery(id+"F7.wireOp",EDGE,"E67")])]})]});}
            var Q5;
            Q5=makeQuery(id+"F8.boolean.opBoolean","INTERSECT",EDGE,{"disambiguationData":[OD(0.0)],"derivedFrom":[makeQuery(id+"F5.opExtrude","SWEPT_FACE",FACE,{"disambiguationData":[OSD([sQuery(id+"F4.wireOp",EDGE,"E30")])]}),makeQuery(id+"F8.opExtrude","SWEPT_FACE",FACE,{"disambiguationData":[OSD([sQuery(id+"F7.wireOp",EDGE,"E67")])]})]});
            fillet(context, id + "F14", {"entities" : qUnion([Q0, Q1, Q2, Q3, Q4, Q5]), "radius" : 3 * mm, "tangentPropagation" : true, "allowEdgeOverflow" : false});
        }
        {
            var Q0;
            Q0=makeQuery(id+"F1.opExtrude","CAP_EDGE",EDGE,{"disambiguationData":[OSD([sQuery(id+"F0.wireOp",EDGE,"E1.bottom")])],"isStart":false});
            fillet(context, id + "F15", {"entities" : qUnion([Q0]), "radius" : 2 * mm, "tangentPropagation" : true, "allowEdgeOverflow" : false});
        }
        {
            var Q0;
            {var subQ0=sQuery(id+"F0.wireOp",EDGE,"E1.bottom");var subQ1=sQuery(id+"F0.wireOp",EDGE,"E1.top");var subQ2=sQuery(id+"F0.wireOp",EDGE,"E1.left");var subQ3=sQuery(id+"F0.wireOp",EDGE,"E1.right");var subQ4=sQuery(id+"F0.wireOp",EDGE,"E4");var subQ5=sQuery(id+"F0.wireOp",EDGE,"E5");var subQ6=sQuery(id+"F0.wireOp",EDGE,"E6");var subQ7=sQuery(id+"F0.wireOp",EDGE,"E7");var subQ8=sQuery(id+"F0.wireOp",EDGE,"E21.filletArc");var subQ9=sQuery(id+"F0.wireOp",EDGE,"E22.filletArc");var subQ10=sQuery(id+"F0.wireOp",EDGE,"E23.filletArc");var subQ11=sQuery(id+"F0.wireOp",EDGE,"E24.filletArc");Q0=makeQuery(id+"F2.boolean.opBoolean","SPLIT",FACE,{"disambiguationData":[TD([makeQuery(id+"F1.opExtrude","SWEPT_FACE",FACE,{"disambiguationData":[OSD([subQ0])]})])],"derivedFrom":makeQuery(id+"F1.opExtrude","CAP_FACE",FACE,{"disambiguationData":[OSD([subQ0,subQ1,subQ2,subQ3,subQ4,subQ5,subQ6,subQ7,subQ8,subQ9,subQ10,subQ11])],"isStart":true})});}
            var sketch = newSketch(context, id + "F16", { "sketchPlane" : qUnion([Q0])});
            skLineSegment(sketch, "E79", {"start": v(88.3, 176.88) * mm, "end": v(88.3, 206.88) * mm, "construction": true});
            skCircle(sketch, "E80", {"center": v(88.3, 206.88) * mm, "radius": 6 * mm});
            skLineSegment(sketch, "E81", {"start": v(103.3, 206.88) * mm, "end": v(103.3, 194.88) * mm});
            skLineSegment(sketch, "E82", {"start": v(103.3, 194.88) * mm, "end": v(121.3, 176.88) * mm});
            skLineSegment(sketch, "E83", {"start": v(73.3, 206.88) * mm, "end": v(73.3, 194.88) * mm});
            skLineSegment(sketch, "E84", {"start": v(73.3, 194.88) * mm, "end": v(55.3, 176.88) * mm});
            skArc(sketch, "E85", {"start": v(103.3, 206.88) * mm, "mid": v(88.3, 221.88) * mm, "end": v(73.3, 206.88) * mm});
            skLineSegment(sketch, "E86.0", {"start": v(162.55, 38.38) * mm, "end": v(162.55, 166.88) * mm});
            skArc(sketch, "E86.1", {"start": v(152.55, 28.38) * mm, "mid": v(159.62, 31.31) * mm, "end": v(162.55, 38.38) * mm});
            skLineSegment(sketch, "E86.2", {"start": v(24.05, 28.38) * mm, "end": v(152.55, 28.38) * mm});
            skArc(sketch, "E86.3", {"start": v(14.05, 38.38) * mm, "mid": v(16.98, 31.31) * mm, "end": v(24.05, 28.38) * mm});
            skLineSegment(sketch, "E86.4", {"start": v(14.05, 38.38) * mm, "end": v(14.05, 166.88) * mm});
            skArc(sketch, "E86.5", {"start": v(24.05, 176.88) * mm, "mid": v(16.98, 173.95) * mm, "end": v(14.05, 166.88) * mm});
            skLineSegment(sketch, "E86.6", {"start": v(24.05, 176.88) * mm, "end": v(152.55, 176.88) * mm});
            skArc(sketch, "E86.7", {"start": v(162.55, 166.88) * mm, "mid": v(159.62, 173.95) * mm, "end": v(152.55, 176.88) * mm});
            skCircle(sketch, "E87.1", {"center": v(148.3, 162.63) * mm, "radius": 4 * mm});
            skCircle(sketch, "E87.2", {"center": v(148.3, 42.63) * mm, "radius": 4 * mm});
            skCircle(sketch, "E87.3", {"center": v(28.3, 42.63) * mm, "radius": 4 * mm});
            skCircle(sketch, "E87.4", {"center": v(28.3, 162.63) * mm, "radius": 4 * mm});
            skArc(sketch, "E88.0", {"start": v(34.04, 54.75) * mm, "mid": v(88.3, 42.63) * mm, "end": v(142.56, 54.75) * mm});
            skArc(sketch, "E88.1", {"start": v(142.56, 54.75) * mm, "mid": v(146.74, 58.44) * mm, "end": v(148.3, 63.8) * mm});
            skLineSegment(sketch, "E88.2", {"start": v(148.3, 141.46) * mm, "end": v(148.3, 63.8) * mm});
            skArc(sketch, "E88.3", {"start": v(148.3, 141.46) * mm, "mid": v(146.74, 146.82) * mm, "end": v(142.56, 150.51) * mm});
            skArc(sketch, "E88.4", {"start": v(142.56, 150.51) * mm, "mid": v(88.3, 162.63) * mm, "end": v(34.04, 150.51) * mm});
            skArc(sketch, "E88.5", {"start": v(34.04, 150.51) * mm, "mid": v(29.86, 146.82) * mm, "end": v(28.3, 141.46) * mm});
            skLineSegment(sketch, "E88.6", {"start": v(28.3, 141.46) * mm, "end": v(28.3, 63.8) * mm});
            skArc(sketch, "E88.7", {"start": v(28.3, 63.8) * mm, "mid": v(29.86, 58.44) * mm, "end": v(34.04, 54.75) * mm});
            skLineSegment(sketch, "E89", {"start": v(14.05, 102.63) * mm, "end": v(162.55, 102.63) * mm, "construction": true});
            skArc(sketch, "E90.MirrorCS", {"start": v(73.3, 206.88) * mm, "mid": v(88.3, 221.88) * mm, "end": v(103.3, 206.88) * mm});
            skLineSegment(sketch, "E91.MirrorCS", {"start": v(103.3, -1.62) * mm, "end": v(103.3, 10.38) * mm});
            skCircle(sketch, "E92.MirrorC", {"center": v(88.3, -1.62) * mm, "radius": 6 * mm});
            skLineSegment(sketch, "E93.MirrorCS", {"start": v(73.3, 10.38) * mm, "end": v(55.3, 28.38) * mm});
            skArc(sketch, "E94.MirrorCS", {"start": v(103.3, -1.62) * mm, "mid": v(88.3, -16.62) * mm, "end": v(73.3, -1.62) * mm});
            skLineSegment(sketch, "E95.MirrorCS", {"start": v(103.3, 10.38) * mm, "end": v(121.3, 28.38) * mm});
            skLineSegment(sketch, "E96.MirrorCS", {"start": v(73.3, -1.62) * mm, "end": v(73.3, 10.38) * mm});
            skLineSegment(sketch, "E97.MirrorCS", {"start": v(88.3, 28.38) * mm, "end": v(88.3, -1.62) * mm, "construction": true});
            skArc(sketch, "E98.MirrorCS", {"start": v(73.3, -1.62) * mm, "mid": v(88.3, -16.62) * mm, "end": v(103.3, -1.62) * mm});
            skSolve(sketch);
        }
        {
            var Q0;
            Q0 = qSketchRegion(id + "F16", true);
            var Q1;
            Q1=makeQuery(id+"F2.opExtrude","CAP_FACE",FACE,{"disambiguationData":[OSD([sQuery(id+"F0.wireOp",EDGE,"E12"),sQuery(id+"F0.wireOp",EDGE,"E13"),sQuery(id+"F0.wireOp",EDGE,"E14"),sQuery(id+"F0.wireOp",EDGE,"E15"),sQuery(id+"F0.wireOp",EDGE,"E17.filletArc"),sQuery(id+"F0.wireOp",EDGE,"E18.filletArc"),sQuery(id+"F0.wireOp",EDGE,"E19.filletArc"),sQuery(id+"F0.wireOp",EDGE,"E20.filletArc"),sQuery(id+"F0.wireOp",EDGE,"E25.0"),sQuery(id+"F0.wireOp",EDGE,"E25.1"),sQuery(id+"F0.wireOp",EDGE,"E25.2"),sQuery(id+"F0.wireOp",EDGE,"E25.3"),sQuery(id+"F0.wireOp",EDGE,"E25.4"),sQuery(id+"F0.wireOp",EDGE,"E25.5"),sQuery(id+"F0.wireOp",EDGE,"E25.6"),sQuery(id+"F0.wireOp",EDGE,"E25.7")])],"isStart":false});
            extrude(context, id + "F17", {"entities" : qUnion([Q0]), "operationType" : NewBodyOperationType.ADD, "endBound" : BoundingType.UP_TO_SURFACE, "endBoundEntityFace" : qUnion([Q1]), "depth" : 25 * mm});
        }
    });
